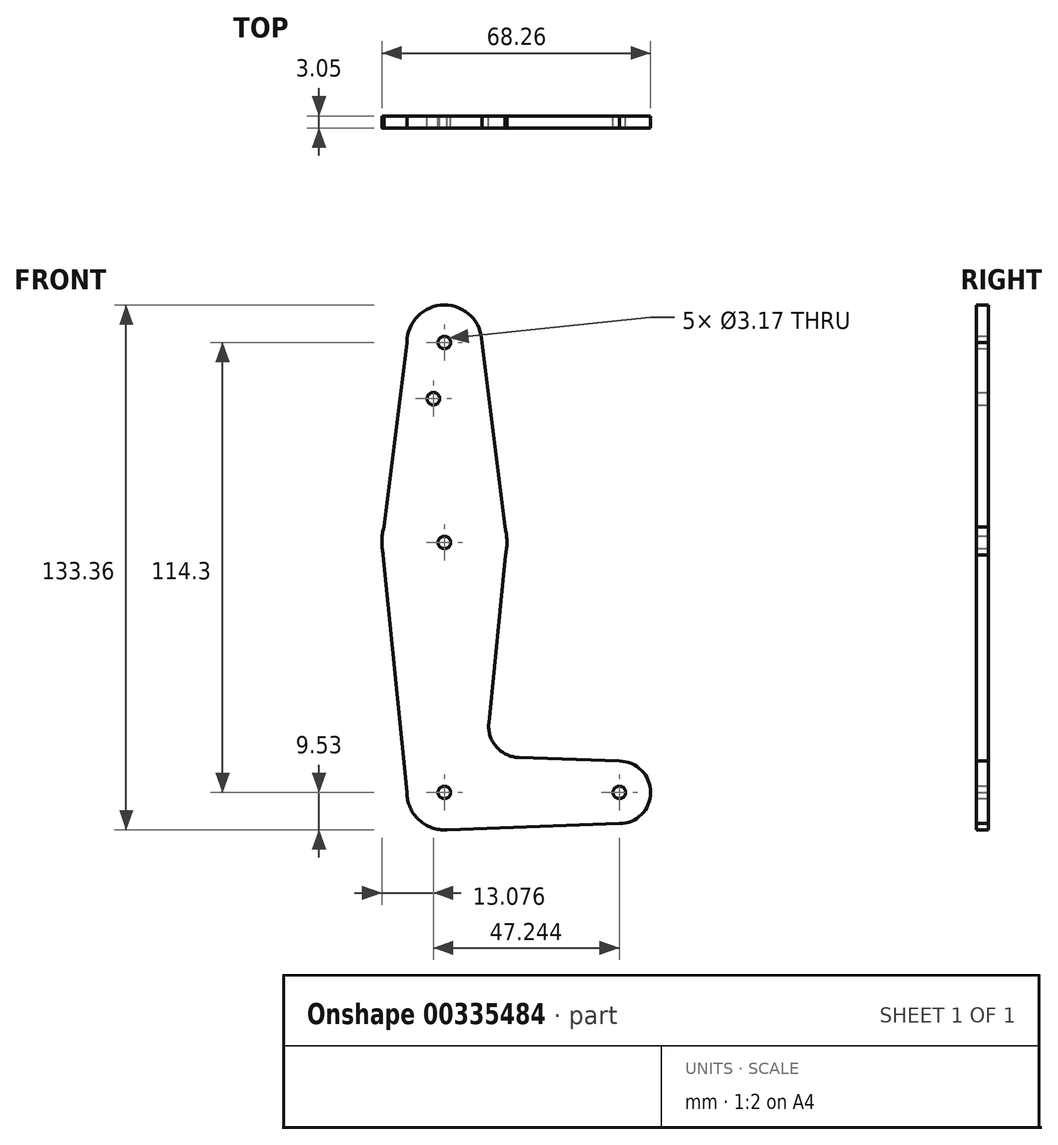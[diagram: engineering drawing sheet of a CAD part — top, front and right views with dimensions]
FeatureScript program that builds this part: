
annotation { "Feature Type Name" : "Feature", "Feature Type Description" : "" }
export const myFeature = defineFeature(function(context is Context, id is Id, definition is map)
    precondition{}
    {
        {
            var Q0;
            Q0=qCreatedBy(makeId("Front.planeOp"),FACE);
            var sketch = newSketch(context, id + "F0", { "sketchPlane" : qUnion([Q0])});
            skCircle(sketch, "E0", {"center": v(0, 0) * mm, "radius": 9.53 * mm});
            skCircle(sketch, "E1", {"center": v(0, 114.3) * mm, "radius": 9.53 * mm});
            skLineSegment(sketch, "E2", {"start": v(0, 0) * mm, "end": v(44.45, 0) * mm});
            skCircle(sketch, "E3", {"center": v(44.45, 0) * mm, "radius": 7.94 * mm});
            skCircle(sketch, "E4", {"center": v(0, 63.5) * mm, "radius": 15.88 * mm});
            skLineSegment(sketch, "E5", {"start": v(-9.52, 114.3) * mm, "end": v(-15.88, 63.5) * mm});
            skLineSegment(sketch, "E6", {"start": v(-15.88, 63.5) * mm, "end": v(-9.52, 0) * mm});
            skLineSegment(sketch, "E7", {"start": v(9.52, 114.3) * mm, "end": v(15.88, 63.5) * mm});
            skLineSegment(sketch, "E8", {"start": v(15.88, 63.5) * mm, "end": v(11.28, 17.59) * mm});
            skLineSegment(sketch, "E9", {"start": v(18.9, 8.85) * mm, "end": v(44.45, 7.94) * mm});
            skLineSegment(sketch, "E10", {"start": v(44.45, -7.94) * mm, "end": v(0, -9.52) * mm});
            skCircle(sketch, "E11", {"center": v(-2.8, 100.03) * mm, "radius": 1.59 * mm});
            skCircle(sketch, "E12", {"center": v(0, 114.3) * mm, "radius": 1.59 * mm});
            skCircle(sketch, "E13", {"center": v(0, 63.5) * mm, "radius": 1.59 * mm});
            skCircle(sketch, "E14", {"center": v(44.45, 0) * mm, "radius": 1.59 * mm});
            skCircle(sketch, "E15", {"center": v(0, 0) * mm, "radius": 1.59 * mm});
            skLineSegment(sketch, "E16", {"start": v(0, 0) * mm, "end": v(0, 114.3) * mm});
            skArc(sketch, "E17.filletArc", {"start": v(11.28, 17.59) * mm, "mid": v(13.2, 11.57) * mm, "end": v(18.9, 8.85) * mm});
            skSolve(sketch);
        }
        {
            var Q0;
            {var subQ0=sQuery(id+"F0.wireOp",EDGE,"E10");var subQ1=sQuery(id+"F0.wireOp",EDGE,"E0");var subQ2=makeQuery(id+"F0.imprint","INTERSECT",VERTEX,{"disambiguationData":[OD(0.0)],"derivedFrom":[subQ1,subQ0]});Q0=makeQuery(id+"F0.imprint","IMPRINT",FACE,{"disambiguationData":[TD([[makeQuery(id+"F0.imprint","IMPRINT",EDGE,{"disambiguationData":[TD([[subQ2,-1.0]])],"derivedFrom":subQ1}),1.0]])]});}
            var Q1;
            {var subQ0=sQuery(id+"F0.wireOp",EDGE,"E7");var subQ1=sQuery(id+"F0.wireOp",EDGE,"E4");var subQ3=makeQuery(id+"F0.imprint","INTERSECT",VERTEX,{"derivedFrom":[subQ1,subQ0]});Q1=makeQuery(id+"F0.imprint","IMPRINT",FACE,{"disambiguationData":[TD([[makeQuery(id+"F0.imprint","IMPRINT",EDGE,{"disambiguationData":[TD([[subQ3,1.0]])],"derivedFrom":subQ1}),1.0]])]});}
            var Q2;
            {var subQ0=sQuery(id+"F0.wireOp",EDGE,"E5");var subQ1=sQuery(id+"F0.wireOp",EDGE,"E4");var subQ3=makeQuery(id+"F0.imprint","INTERSECT",VERTEX,{"derivedFrom":[subQ1,subQ0]});Q2=makeQuery(id+"F0.imprint","IMPRINT",FACE,{"disambiguationData":[TD([[makeQuery(id+"F0.imprint","IMPRINT",EDGE,{"disambiguationData":[TD([[subQ3,-1.0]])],"derivedFrom":subQ1}),1.0]])]});}
            var Q3;
            {var subQ0=sQuery(id+"F0.wireOp",EDGE,"E6");var subQ1=sQuery(id+"F0.wireOp",EDGE,"E4");var subQ3=makeQuery(id+"F0.imprint","INTERSECT",VERTEX,{"derivedFrom":[subQ1,subQ0]});Q3=makeQuery(id+"F0.imprint","IMPRINT",FACE,{"disambiguationData":[TD([[makeQuery(id+"F0.imprint","IMPRINT",EDGE,{"disambiguationData":[TD([[subQ3,1.0]])],"derivedFrom":subQ1}),1.0]])]});}
            var Q4;
            {var subQ0=sQuery(id+"F0.wireOp",EDGE,"E8");var subQ1=sQuery(id+"F0.wireOp",EDGE,"E4");var subQ3=makeQuery(id+"F0.imprint","INTERSECT",VERTEX,{"derivedFrom":[subQ1,subQ0]});Q4=makeQuery(id+"F0.imprint","IMPRINT",FACE,{"disambiguationData":[TD([[makeQuery(id+"F0.imprint","IMPRINT",EDGE,{"disambiguationData":[TD([[subQ3,-1.0]])],"derivedFrom":subQ1}),1.0]])]});}
            var Q5;
            {var subQ0=sQuery(id+"F0.wireOp",EDGE,"E6");var subQ1=sQuery(id+"F0.wireOp",EDGE,"E0");var subQ2=makeQuery(id+"F0.imprint","INTERSECT",VERTEX,{"derivedFrom":[subQ1,subQ0]});Q5=makeQuery(id+"F0.imprint","IMPRINT",FACE,{"disambiguationData":[TD([[makeQuery(id+"F0.imprint","IMPRINT",EDGE,{"disambiguationData":[TD([[subQ2,1.0]])],"derivedFrom":subQ1}),-1.0]])]});}
            var Q6;
            {var subQ0=sQuery(id+"F0.wireOp",EDGE,"E10");var subQ1=sQuery(id+"F0.wireOp",EDGE,"E0");var subQ2=makeQuery(id+"F0.imprint","INTERSECT",VERTEX,{"disambiguationData":[OD(1.0)],"derivedFrom":[subQ1,subQ0]});Q6=makeQuery(id+"F0.imprint","IMPRINT",FACE,{"disambiguationData":[TD([[makeQuery(id+"F0.imprint","IMPRINT",EDGE,{"disambiguationData":[TD([[subQ2,-1.0]])],"derivedFrom":subQ1}),-1.0]])]});}
            var Q7;
            Q7=makeQuery(id+"F0.imprint","IMPRINT",FACE,{"disambiguationData":[TD([[makeQuery(id+"F0.imprint","IMPRINT",EDGE,{"derivedFrom":sQuery(id+"F0.wireOp",EDGE,"E12")}),-1.0]])]});
            var Q8;
            Q8=makeQuery(id+"F0.imprint","IMPRINT",FACE,{"disambiguationData":[TD([[makeQuery(id+"F0.imprint","IMPRINT",EDGE,{"derivedFrom":sQuery(id+"F0.wireOp",EDGE,"E14")}),-1.0]])]});
            var Q9;
            {var subQ0=sQuery(id+"F0.wireOp",EDGE,"E9");Q9=makeQuery(id+"F0.imprint","IMPRINT",FACE,{"disambiguationData":[TD([[makeQuery(id+"F0.imprint","IMPRINT",EDGE,{"derivedFrom":subQ0}),-1.0]])]});}
            var Q10;
            {var subQ1=sQuery(id+"F0.wireOp",EDGE,"E0");var subQ7=makeQuery(id+"F0.imprint","INTERSECT",VERTEX,{"derivedFrom":[subQ1,sQuery(id+"F0.wireOp",EDGE,"E6")]});Q10=makeQuery(id+"F0.imprint","IMPRINT",FACE,{"disambiguationData":[TD([[makeQuery(id+"F0.imprint","IMPRINT",EDGE,{"disambiguationData":[TD([[subQ7,1.0]])],"derivedFrom":subQ1}),1.0]])]});}
            var Q11;
            {var subQ1=sQuery(id+"F0.wireOp",EDGE,"E7");var subQ2=sQuery(id+"F0.wireOp",EDGE,"E4");var subQ5=makeQuery(id+"F0.imprint","INTERSECT",VERTEX,{"derivedFrom":[subQ2,subQ1]});Q11=makeQuery(id+"F0.imprint","IMPRINT",FACE,{"disambiguationData":[TD([[makeQuery(id+"F0.imprint","IMPRINT",EDGE,{"disambiguationData":[TD([[subQ5,-1.0]])],"derivedFrom":subQ2}),1.0]])]});}
            var Q12;
            {var subQ1=sQuery(id+"F0.wireOp",EDGE,"E5");var subQ2=sQuery(id+"F0.wireOp",EDGE,"E4");var subQ4=makeQuery(id+"F0.imprint","INTERSECT",VERTEX,{"derivedFrom":[subQ2,subQ1]});Q12=makeQuery(id+"F0.imprint","IMPRINT",FACE,{"disambiguationData":[TD([[makeQuery(id+"F0.imprint","IMPRINT",EDGE,{"disambiguationData":[TD([[subQ4,1.0]])],"derivedFrom":subQ2}),1.0]])]});}
            var Q13;
            Q13=makeQuery(id+"F0.imprint","IMPRINT",FACE,{"disambiguationData":[TD([[makeQuery(id+"F0.imprint","IMPRINT",EDGE,{"derivedFrom":sQuery(id+"F0.wireOp",EDGE,"E11")}),-1.0]])]});
            var Q14;
            {var subQ0=sQuery(id+"F0.wireOp",EDGE,"E7");var subQ1=sQuery(id+"F0.wireOp",EDGE,"E1");var subQ2=makeQuery(id+"F0.imprint","INTERSECT",VERTEX,{"derivedFrom":[subQ1,subQ0]});Q14=makeQuery(id+"F0.imprint","IMPRINT",FACE,{"disambiguationData":[TD([[makeQuery(id+"F0.imprint","IMPRINT",EDGE,{"disambiguationData":[TD([[subQ2,1.0]])],"derivedFrom":subQ1}),-1.0]])]});}
            var Q15;
            {var subQ0=sQuery(id+"F0.wireOp",EDGE,"E16");var subQ1=sQuery(id+"F0.wireOp",EDGE,"E0");var subQ2=makeQuery(id+"F0.imprint","INTERSECT",VERTEX,{"derivedFrom":[subQ1,subQ0]});Q15=makeQuery(id+"F0.imprint","IMPRINT",FACE,{"disambiguationData":[TD([[makeQuery(id+"F0.imprint","IMPRINT",EDGE,{"disambiguationData":[TD([[subQ2,1.0]])],"derivedFrom":subQ1}),1.0]])]});}
            extrude(context, id + "F1", {"entities" : qUnion([Q0, Q1, Q2, Q3, Q4, Q5, Q6, Q7, Q8, Q9, Q10, Q11, Q12, Q13, Q14, Q15]), "depth" : 3.05 * mm});
        }
    });
